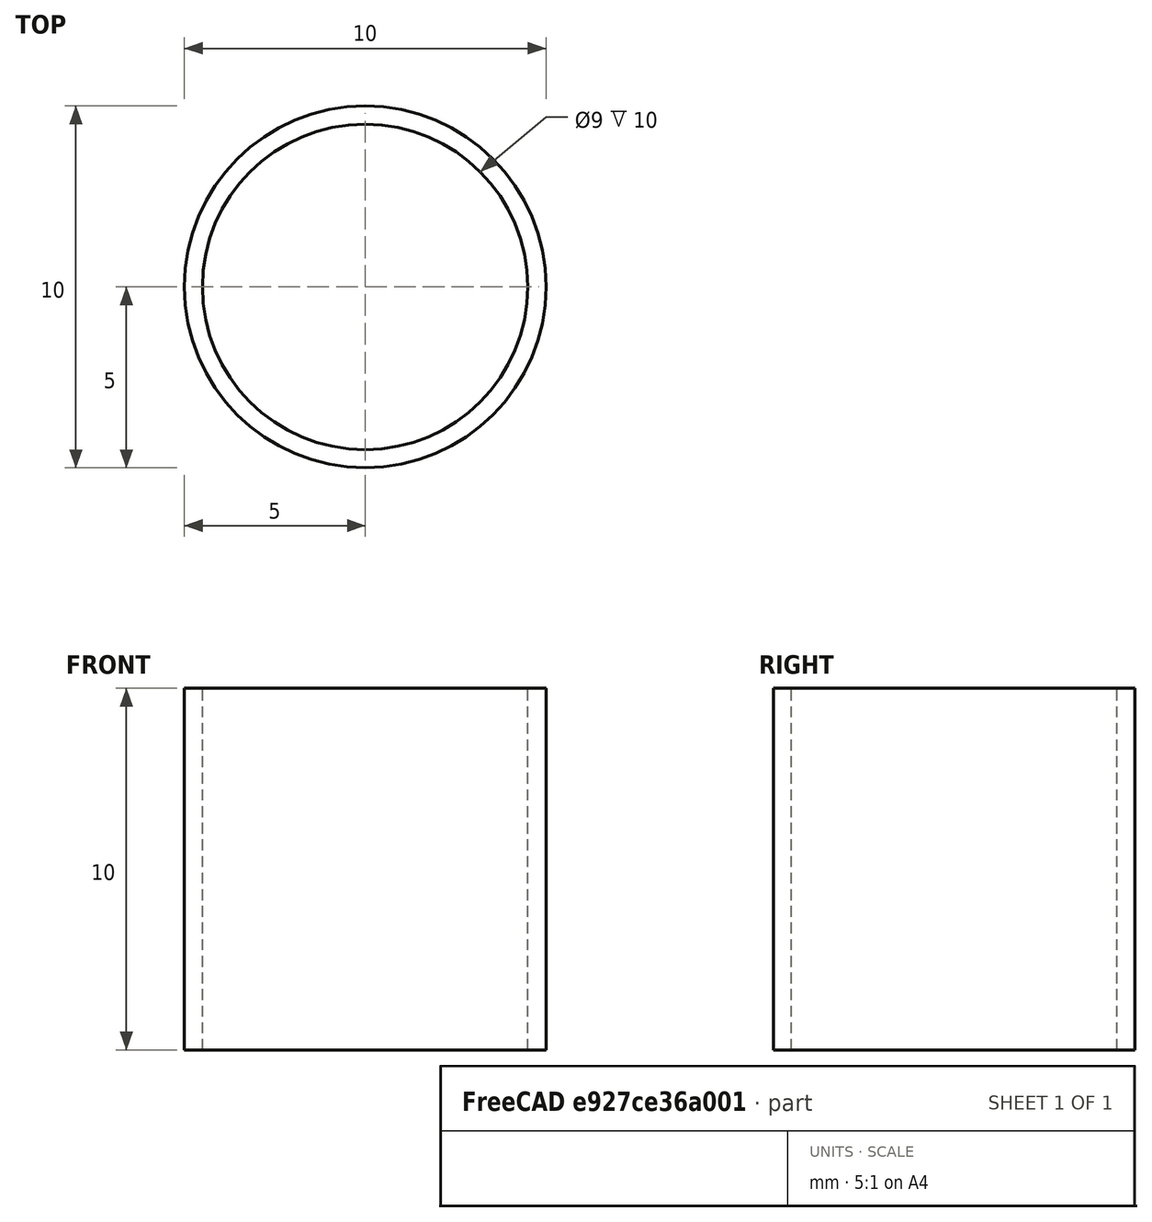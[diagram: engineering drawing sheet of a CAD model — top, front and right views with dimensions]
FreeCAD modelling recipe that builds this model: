
FCSTD DOCUMENT  (FreeCAD 0.17R11508 (Git))
Label: test_cyl_in_tube
License: All rights reserved
LicenseURL: http://en.wikipedia.org/wiki/All_rights_reserved
objects: Part::Cylinder×3, Fem::FemSolverObjectPython×2, Fem::FemMeshObjectPython×2, Fem::FemAnalysisPython×2, Part::Cut×1, Fem::ConstraintContact×1, Fem::ConstraintDisplacement×1
note: 4 computed .brp shape members not serialized (recipe doc carries the construction recipe); baked Part::Feature solids carry a one-line shape summary decoded from their .brp

FEATURE [Part::Cylinder] Cylinder
  Angle = 360
  AttacherType = Attacher::AttachEngine3D
  Height = 10
  Radius = 5
FEATURE [Part::Cylinder] Cylinder001
  Angle = 360
  AttacherType = Attacher::AttachEngine3D
  Height = 10
  Radius = 4.5
FEATURE [Part::Cut] Cut
  Base = -> Cylinder
  Tool = -> Cylinder001
FEATURE [Part::Cylinder] Cylinder002
  Angle = 360
  AttacherType = Attacher::AttachEngine3D
  Height = 10
  Radius = 4.5
FEATURE [Fem::ConstraintContact] FemConstraintContact
  Friction = 0
  NormalDirection = (1,0,0)
  Normals = (24) [(-1,0,0),(0.5,-0.866025,0),(0.5,0.866025,0),(-1,2.44929e-16,0),(-1,0,0),(0.5,-0.866025,0),(0.5,0.866025,0),(-1,2.44929e-16,0),(-1,0,0),+15 more]
  Points = (24) [(4.5,0,0),(-2.25,3.89711,0),(-2.25,-3.89711,0),(4.5,-1.10218e-15,0),(4.5,0,5),(-2.25,3.89711,5),(-2.25,-3.89711,5),(4.5,-1.10218e-15,5),(4.5,0,10),+15 more]
  References = -> [Cut,Cylinder002]
  Slope = 1000000
FEATURE [Fem::FemSolverObjectPython] CalculiX  # FEM object (typed FeaturePython)
  AnalysisType = 0
  EigenmodeHighLimit = 1000000
  EigenmodeLowLimit = 0
  EigenmodesCount = 10
  GeometricalNonlinearity = 0
  IterationsControlParameterCutb = 0.25,0.5,0.75,0.85,,,1.5,
  IterationsControlParameterIter = 4,8,9,200,10,400,,200,,
  IterationsControlParameterTimeUse = false
  IterationsThermoMechMaximum = 2000
  IterationsUserDefinedIncrementations = false
  IterationsUserDefinedTimeStepLength = false
  MaterialNonlinearity = 0
  MatrixSolverType = 0
  SolverType = FemSolverCalculix
  SplitInputWriter = false
  ThermoMechSteadyState = true
  TimeEnd = 1
  TimeInitialStep = 0.01
FEATURE [Fem::FemMeshObjectPython] FEMMeshGMSH001  # FEM object (typed FeaturePython)
  Algorithm2D = 0
  Algorithm3D = 0
  CharacteristicLengthMax = 0
  CharacteristicLengthMin = 0
  CoherenceMesh = true
  ElementDimension = 0
  ElementOrder = 1
  GeometryTolerance = 1e-06
  HighOrderOptimize = false
  OptimizeNetgen = false
  OptimizeStd = true
  Part = -> Cut
  RecombineAll = false
FEATURE [Fem::FemMeshObjectPython] FEMMeshGMSH  # FEM object (typed FeaturePython)
  Algorithm2D = 0
  Algorithm3D = 0
  CharacteristicLengthMax = 0
  CharacteristicLengthMin = 0
  CoherenceMesh = true
  ElementDimension = 0
  ElementOrder = 1
  GeometryTolerance = 1e-06
  HighOrderOptimize = false
  OptimizeNetgen = false
  OptimizeStd = true
  Part = -> Cylinder002
  RecombineAll = false
FEATURE [Fem::FemSolverObjectPython] CalculiX001  # FEM object (typed FeaturePython)
  AnalysisType = 0
  EigenmodeHighLimit = 1000000
  EigenmodeLowLimit = 0
  EigenmodesCount = 10
  GeometricalNonlinearity = 0
  IterationsControlParameterCutb = 0.25,0.5,0.75,0.85,,,1.5,
  IterationsControlParameterIter = 4,8,9,200,10,400,,200,,
  IterationsControlParameterTimeUse = false
  IterationsThermoMechMaximum = 2000
  IterationsUserDefinedIncrementations = false
  IterationsUserDefinedTimeStepLength = false
  MaterialNonlinearity = 0
  MatrixSolverType = 0
  SolverType = FemSolverCalculix
  SplitInputWriter = false
  ThermoMechSteadyState = true
  TimeEnd = 1
  TimeInitialStep = 0.01
FEATURE [Fem::FemAnalysisPython] Analysis001  # FEM object (typed FeaturePython)
  Member = -> [CalculiX001]
FEATURE [Fem::ConstraintDisplacement] FemConstraintDisplacement
  NormalDirection = (0,0,1)
  Normals = (5) [(0,0,1),(0,0,1),(0,0,1),(0,0,1),(0,0,1)]
  Points = (5) [(0,-4.5,10),(-4.5,0,10),(0,0,10),(4.5,0,10),(0,4.5,10)]
  References = -> [Cylinder002]
  rotxFix = false
  rotxFree = true
  rotyFix = false
  rotyFree = true
  rotzFix = false
  rotzFree = true
  xDisplacement = 0
  xFix = false
  xFree = true
  xRotation = 0
  yDisplacement = 10
  yFix = false
  yFree = false
  yRotation = 0
  zDisplacement = 0
  zFix = false
  zFree = true
  zRotation = 0
FEATURE [Fem::FemAnalysisPython] Analysis  # FEM object (typed FeaturePython)
  Member = -> [CalculiX,FemConstraintContact,FEMMeshGMSH001,FEMMeshGMSH,FemConstraintDisplacement]
